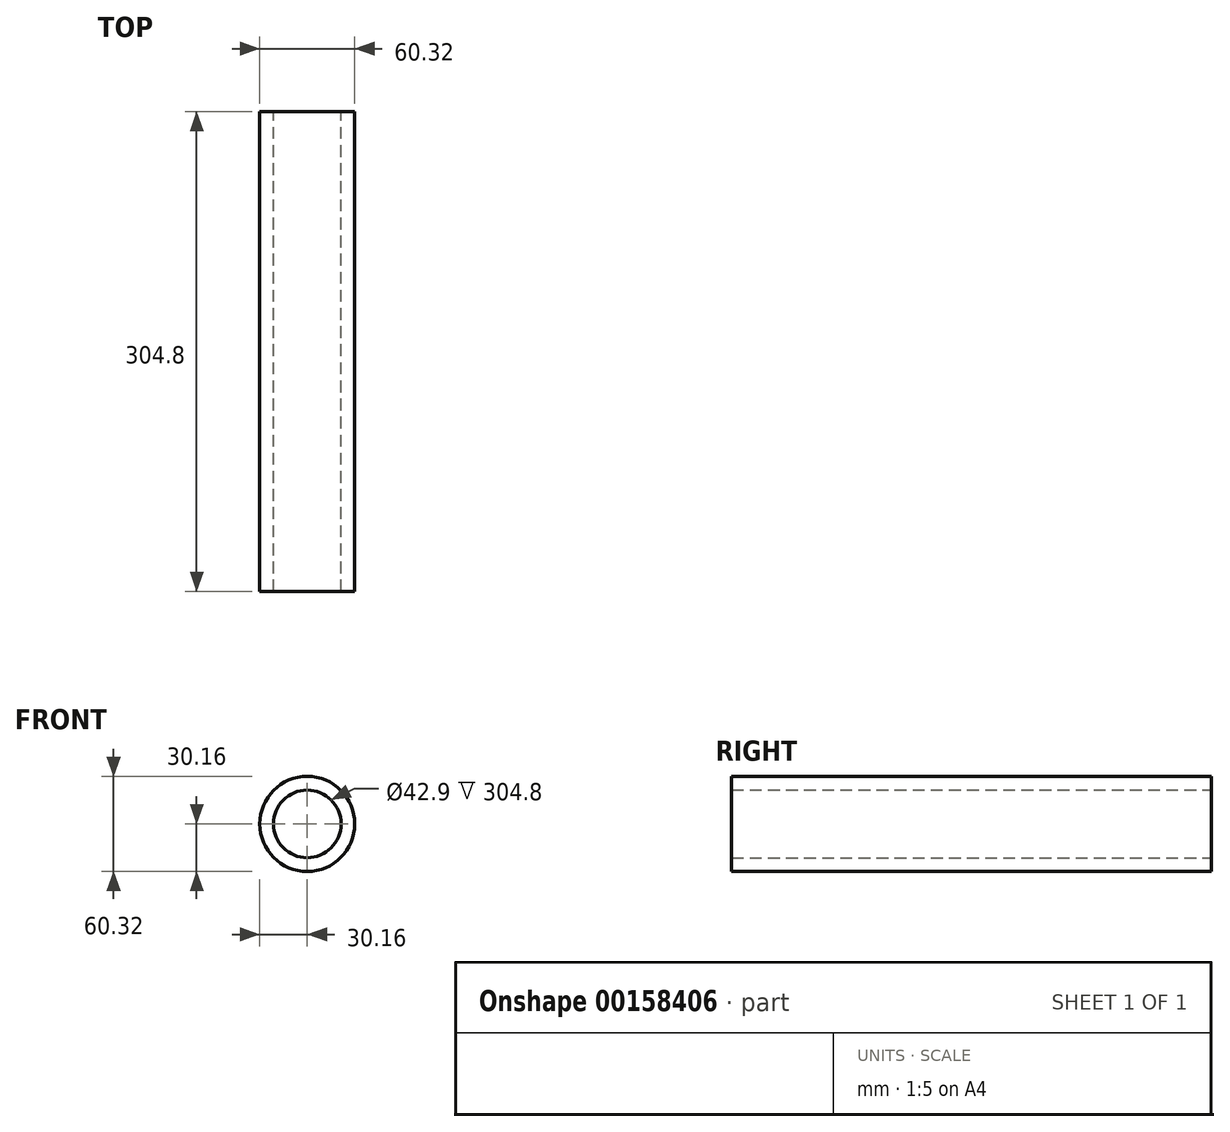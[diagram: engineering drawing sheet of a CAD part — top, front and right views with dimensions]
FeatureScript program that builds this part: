
annotation { "Feature Type Name" : "Feature", "Feature Type Description" : "" }
export const myFeature = defineFeature(function(context is Context, id is Id, definition is map)
    precondition{}
    {
        {
            var Q0;
            Q0=qCreatedBy(makeId("Front.planeOp"),FACE);
            var sketch = newSketch(context, id + "F0", { "sketchPlane" : qUnion([Q0])});
            skCircle(sketch, "E0", {"center": v(0, 0) * mm, "radius": 30.16 * mm});
            skCircle(sketch, "E1.0", {"center": v(0, 0) * mm, "radius": 21.45 * mm});
            skSolve(sketch);
        }
        {
            var Q0;
            Q0=makeQuery(id+"F0.imprint","IMPRINT",FACE,{"disambiguationData":[TD([[makeQuery(id+"F0.imprint","IMPRINT",EDGE,{"derivedFrom":sQuery(id+"F0.wireOp",EDGE,"E0")}),1.0]])]});
            extrude(context, id + "F1", {"entities" : qUnion([Q0]), "depth" : 304.8 * mm});
        }
    });
